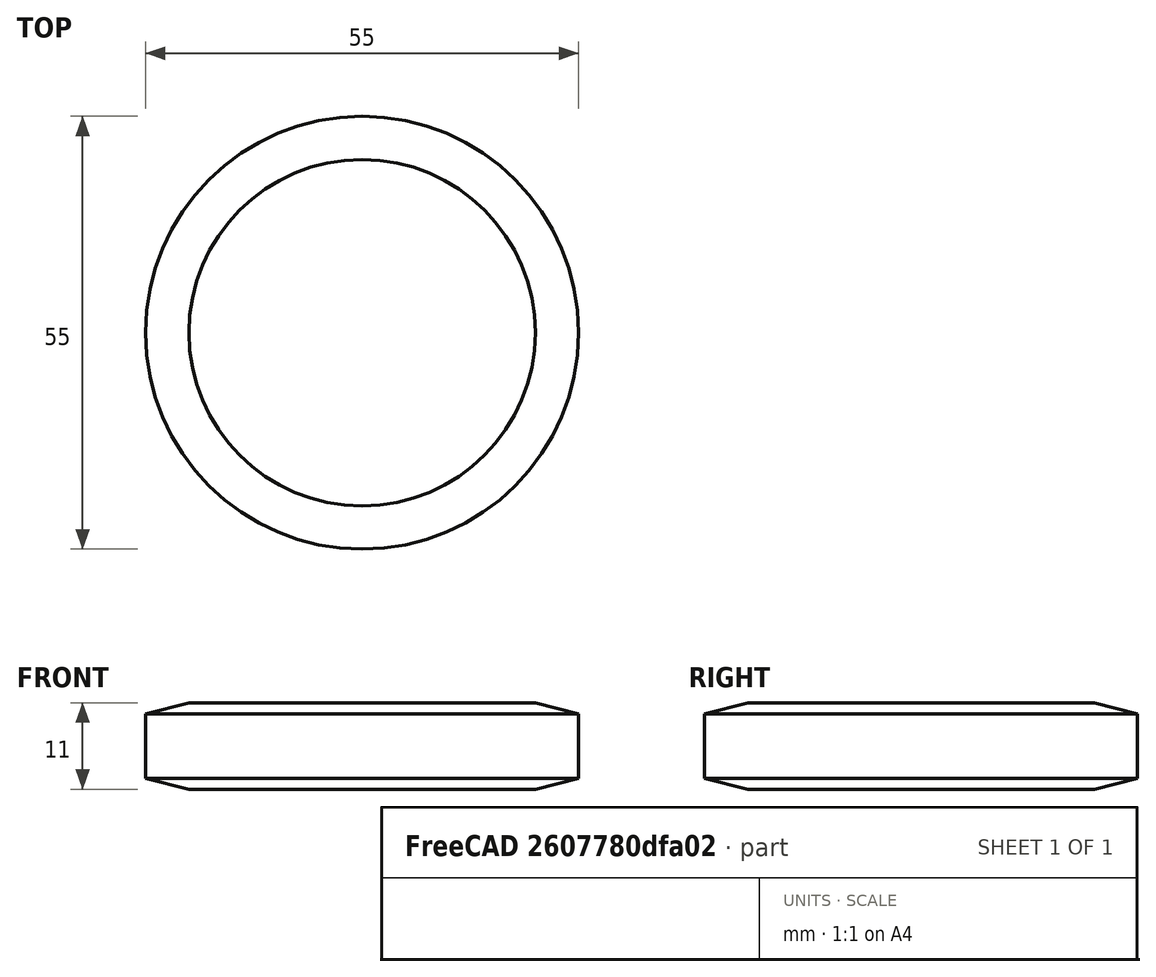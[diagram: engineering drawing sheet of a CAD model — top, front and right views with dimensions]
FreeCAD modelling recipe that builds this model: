
FCSTD DOCUMENT  (FreeCAD 1.0R1.0.0)
Label: KFFlangeClamp
License: All rights reserved
LicenseURL: http://en.wikipedia.org/wiki/All_rights_reserved
objects: Part::Cone×2, Spreadsheet::Sheet×1, Part::Cylinder×1, Part::MultiFuse×1
note: 4 computed .brp shape members not serialized (recipe doc carries the construction recipe); baked Part::Feature solids carry a one-line shape summary decoded from their .brp

FEATURE [Spreadsheet::Sheet] Spreadsheet  label="KleinFlange"
  KF = 3
  cells = A1='Nominal bore; B1='D: O-ring ID; C1='d1: Pipe OD; D1='d2: Carrier retainer diameter; E1='d3: Coupling OD; F1='d4: Carrier ID; G1='d5: Connecting Pipe Carrier OD; H1='d6: OD to hold Oring in carrier; I1='R: O ring retainer radius (carrier); A2==hiddenref(.KF.String); B2(D)==.B6; C2(d1)==.C6; D2(d2)==.D6; E2(d3)==.E6; F2(d4)==.F6; G2(d5)==.G6; H2(d6)==.H6; I2(R)=; A3='10; B3=15; C3=14; D3=12.2; E3=30; F3=10; G3=12; H3=15.3; A4='16; B4=18; C4=20; D4=17.2; E4=30; F4=16; G4=17; H4=18.5; A5='25; B5=28; C5=28; D5=26.2; E5=40; F5=25; G5=26; H5=28.5; A6='40; B6=42; C6=44.5; D6=41.2; E6=55; F6=40; G6=41; H6=43; A7='50; B7=55; C7=61; D7=52.2; E7=75; F7=50; G7=52; H7=55.5; A9='O Ring; A10='O ring diameter; B10(oring_dia)=5; A11='Inner diameter; B11==B2; A13='Coupling; L13='Coupling calculated properties; A14='Total length; B14(coupling_len)=10; C14='10 is minimum length; L14='Taper height; M14(coupling_taper_height)==(d3 - d1) / (2 * tan(90 - 15)); A15='Pipe diameter; B15(pipe_dia_user)=100; C15='Maximum specified by d5 (Connecting pipe diameter); L15='Effective pipe diameter; M15(coupling_pipe_ID)==min(d5; pipe_dia_user); L16='Effective coupling length; M16(coupling_len_eff)==min(coupling_len; 10); A17='Clamp; L17='Clamp calculated properties; L18='Clamp taper height; M18(clamp_taper_height)==(oring_dia + 0.5) / (2 * tan(90 - 15))
  expr: .KF.Enum = cells[<<A3:|>>]
  expr: .cells.Bind.B2.I2 = tuple(.cells; <<B>> + str(hiddenref(KF) + 3); <<I>> + str(hiddenref(KF) + 3))
FEATURE [Part::Cone] Cone
  Angle = 360
  AttacherType = Attacher::AttachEngine3D
  Height = 1.40673
  Placement = pos=(0,0,4.09327) rot=(1,0,0;0rad)
  Radius1 = 27.5
  Radius2 = 22
  expr: .Placement.Base.z = (<<KleinFlange>>.oring_dia + 2 * 3 - 2 * <<KleinFlange>>.coupling_taper_height) / 2
  expr: Height = <<KleinFlange>>.coupling_taper_height
  expr: Radius1 = <<KleinFlange>>.d3 / 2
  expr: Radius2 = <<KleinFlange>>.d3 / 2 - <<KleinFlange>>.oring_dia - 0.5
FEATURE [Part::Cylinder] Cylinder
  Angle = 360
  AttacherType = Attacher::AttachEngine3D
  FirstAngle = 0
  Height = 8.18653
  Placement = pos=(0,0,-4.09327) rot=(0,0,1;0rad)
  Radius = 27.5
  SecondAngle = 0
  expr: .Placement.Base.z = -(<<KleinFlange>>.oring_dia + 2 * 3 - 2 * <<KleinFlange>>.coupling_taper_height) / 2
  expr: Height = <<KleinFlange>>.oring_dia + 2 * 3 - 2 * <<KleinFlange>>.coupling_taper_height
  expr: Radius = <<KleinFlange>>.d3 / 2
FEATURE [Part::Cone] Cone001
  Angle = 360
  AttacherType = Attacher::AttachEngine3D
  Height = 1.40673
  Placement = pos=(0,0,-5.5) rot=(0,0,1;0rad)
  Radius1 = 22
  Radius2 = 27.5
  expr: .Placement.Base.z = -((<<KleinFlange>>.oring_dia + 2 * 3 - 2 * <<KleinFlange>>.coupling_taper_height) / 2) - <<KleinFlange>>.coupling_taper_height
  expr: Height = <<KleinFlange>>.coupling_taper_height
  expr: Radius1 = <<KleinFlange>>.d3 / 2 - <<KleinFlange>>.oring_dia - 0.5
  expr: Radius2 = <<KleinFlange>>.d3 / 2
FEATURE [Part::MultiFuse] Fusion  label="KFTemplate_Narrow"
  Shapes = -> [Cone,Cylinder,Cone001]
